# Revit family: EKF_EE_ДверьFORT_IP31_PROxima
name_source: partatom
category: Электрооборудование
units: mm (PartAtom-declared; Revit-internal decimal feet)

## family parameters
Всегда вертикально = Нет
На основе рабочей плоскости = Да
Общий = Да
При загрузке вырезать с полостями = Нет
Размер круглого соединителя = Использовать диаметр
Тип детали = Силовой щит
Точка расчета площади = Нет

## types (8) — shared parameters
ADSK_Единица измерения = шт.
ADSK_Завод-изготовитель = EKF
ADSK_Количество = 1
ADSK_Марка = Дверь FORT
ADSK_Материал = RAL 7035_Сталь
ADSK_Обозначение = Дверь FORT
ADSK_Размер_Глубина = 21 мм
Изготовитель = EKF
КолОтв = 4
Серия номенклатуры = PROxima
Степень защиты IP = IP31
ТВ = EKF_2
Тип установки = -
zero-valued in all types: ADSK_Масса, Отметка по умолчанию

## per-type parameters (varying)
| type | ADSK_Код изделия | ADSK_Размер_Высота | ADSK_Размер_Ширина | Карман для документации | Тип |
| Дверь FORT для корпуса высотой 1800 и шириной 600 IP31 EKF PROxima | FD186 | 1800 мм | 591.5 мм | Да | 372 мм |
| Дверь FORT для корпуса высотой 1800 и шириной 800 IP31 EKF PROxima | FD188 | 1800 мм | 791.5 мм | Да | 374 мм |
| Дверь FORT для корпуса высотой 2000 и шириной 400 IP31 EKF PROxima | FD204 | 2000 мм | 391.5 мм | Нет | 376 мм |
| Дверь FORT для корпуса высотой 2000 и шириной 600 IP31 EKF PROxima | FD206 | 2000 мм | 591.5 мм | Да | 378 мм |
| Дверь FORT для корпуса высотой 2000 и шириной 800 IP31 EKF PROxima | FD208 | 2000 мм | 791.5 мм | Да | 380 мм |
| Дверь FORT для корпуса высотой 2200 и шириной 400 IP31 EKF PROxima | FD224 | 2200 мм | 391.5 мм | Нет | 382 мм |
| Дверь FORT для корпуса высотой 2200 и шириной 600 IP31 EKF PROxima | FD226 | 2200 мм | 591.5 мм | Да | 384 мм |
| Дверь FORT для корпуса высотой 2200 и шириной 800 IP31 EKF PROxima | FD228 | 2200 мм | 791.5 мм | Да | 386 мм |

note: column(s) folded — value = type name in every type: ADSK_Наименование
